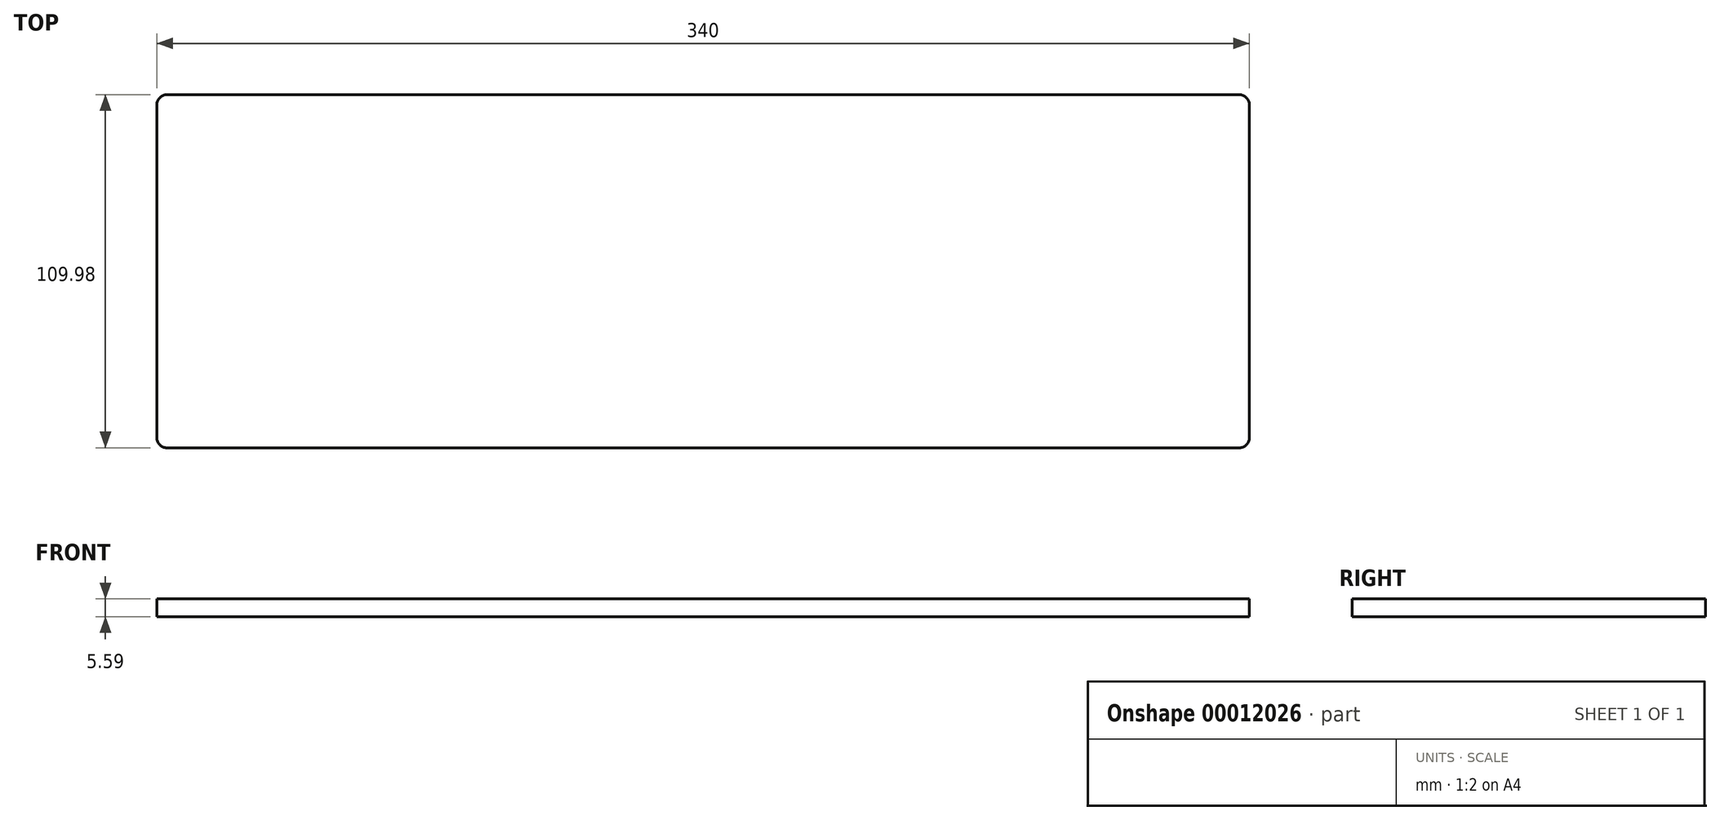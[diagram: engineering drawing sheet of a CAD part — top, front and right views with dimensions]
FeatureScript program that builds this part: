
annotation { "Feature Type Name" : "Feature", "Feature Type Description" : "" }
export const myFeature = defineFeature(function(context is Context, id is Id, definition is map)
    precondition{}
    {
        {
            var Q0;
            Q0=qCreatedBy(makeId("Top.planeOp"),FACE);
            var sketch = newSketch(context, id + "F0", { "sketchPlane" : qUnion([Q0])});
            skLineSegment(sketch, "E0.rect.bottom", {"start": v(170, 55) * mm, "end": v(-170, 55) * mm});
            skLineSegment(sketch, "E0.rect.top", {"start": v(170, -55) * mm, "end": v(-170, -55) * mm});
            skLineSegment(sketch, "E0.rect.left", {"start": v(170, 55) * mm, "end": v(170, -55) * mm});
            skLineSegment(sketch, "E0.rect.right", {"start": v(-170, 55) * mm, "end": v(-170, -55) * mm});
            skPoint(sketch, "E0.rect.middle", {"position": v(0, 0) * mm});
            skSolve(sketch);
        }
        {
            var Q0;
            Q0 = qSketchRegion(id + "F0", true);
            extrude(context, id + "F1", {"entities" : qUnion([Q0]), "depth" : 5.6 * mm});
        }
        {
            var Q0;
            Q0=makeQuery(id+"F1.opExtrude","SWEPT_EDGE",EDGE,{"disambiguationData":[OSD([sQuery(id+"F0.wireOp",EDGE,"E0.rect.top"),sQuery(id+"F0.wireOp",EDGE,"E0.rect.left")])]});
            var Q1;
            Q1=makeQuery(id+"F1.opExtrude","SWEPT_EDGE",EDGE,{"disambiguationData":[OSD([sQuery(id+"F0.wireOp",EDGE,"E0.rect.bottom"),sQuery(id+"F0.wireOp",EDGE,"E0.rect.left")])]});
            var Q2;
            Q2=makeQuery(id+"F1.opExtrude","SWEPT_EDGE",EDGE,{"disambiguationData":[OSD([sQuery(id+"F0.wireOp",EDGE,"E0.rect.top"),sQuery(id+"F0.wireOp",EDGE,"E0.rect.right")])]});
            var Q3;
            Q3=makeQuery(id+"F1.opExtrude","SWEPT_EDGE",EDGE,{"disambiguationData":[OSD([sQuery(id+"F0.wireOp",EDGE,"E0.rect.bottom"),sQuery(id+"F0.wireOp",EDGE,"E0.rect.right")])]});
            fillet(context, id + "F2", {"entities" : qUnion([Q0, Q1, Q2, Q3]), "radius" : 3.17 * mm, "tangentPropagation" : true, "allowEdgeOverflow" : false});
        }
    });
